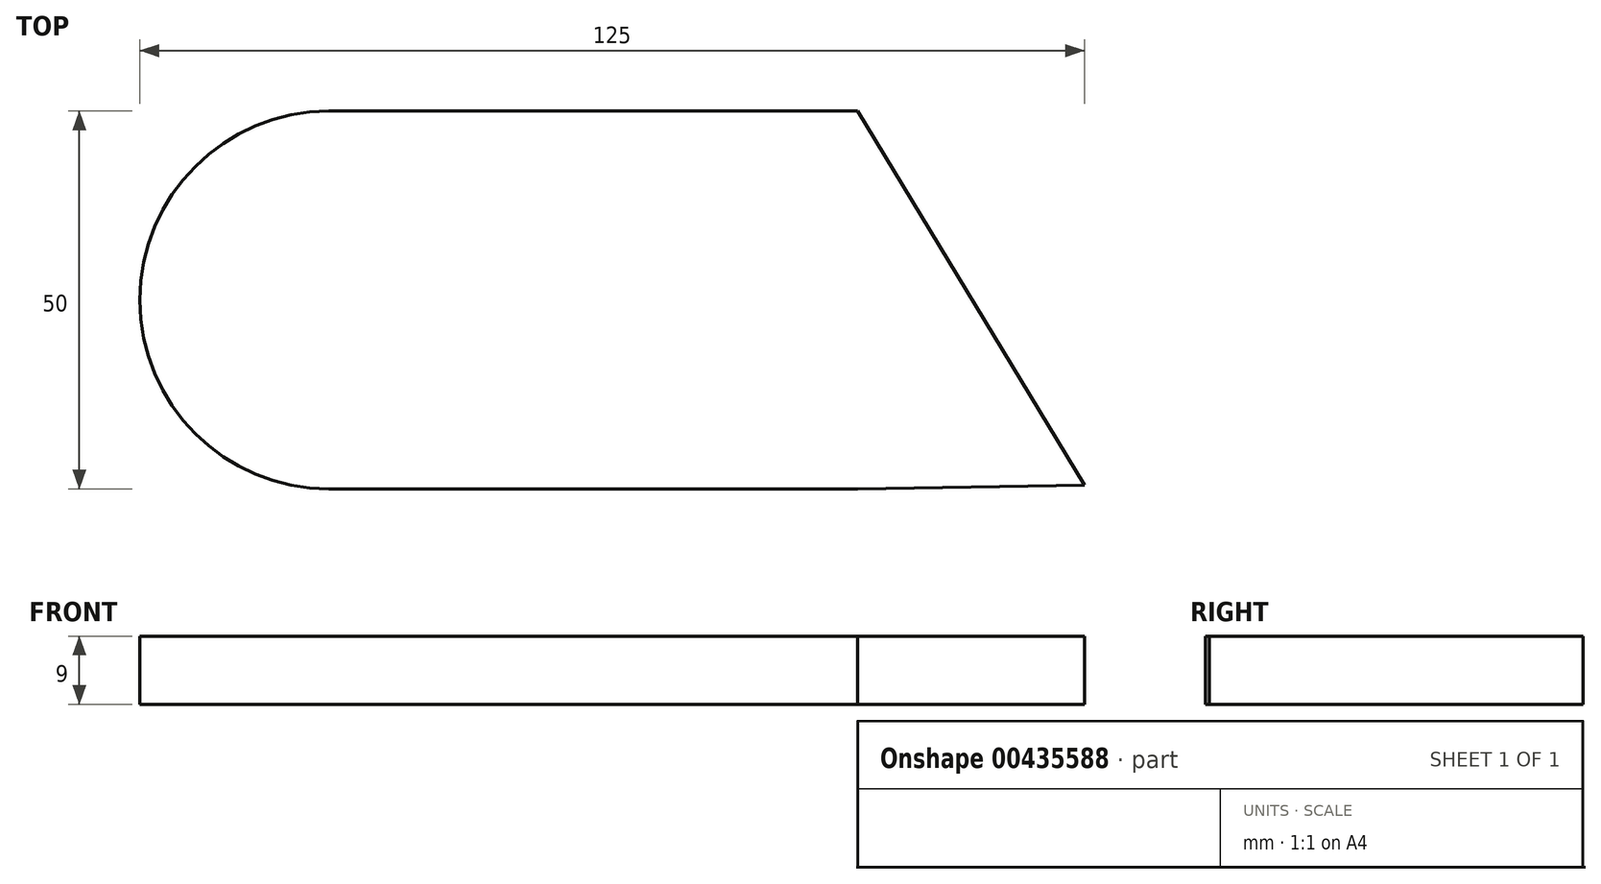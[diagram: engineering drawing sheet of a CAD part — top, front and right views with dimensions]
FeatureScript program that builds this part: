
annotation { "Feature Type Name" : "Feature", "Feature Type Description" : "" }
export const myFeature = defineFeature(function(context is Context, id is Id, definition is map)
    precondition{}
    {
        {
            var Q0;
            Q0=qCreatedBy(makeId("Top.planeOp"),FACE);
            var sketch = newSketch(context, id + "F0", { "sketchPlane" : qUnion([Q0])});
            skLineSegment(sketch, "E0.bottom", {"start": v(-28.66, 56.52) * mm, "end": v(41.34, 56.52) * mm});
            skLineSegment(sketch, "E0.top", {"start": v(-28.66, 6.52) * mm, "end": v(41.34, 6.52) * mm});
            skLineSegment(sketch, "E0.left", {"start": v(-28.66, 56.52) * mm, "end": v(-28.66, 6.52) * mm});
            skLineSegment(sketch, "E0.right", {"start": v(41.34, 56.52) * mm, "end": v(41.34, 6.52) * mm});
            skArc(sketch, "E1", {"start": v(-28.66, 56.52) * mm, "mid": v(-53.66, 31.52) * mm, "end": v(-28.66, 6.52) * mm});
            skLineSegment(sketch, "E2", {"start": v(41.34, 56.52) * mm, "end": v(71.34, 7.03) * mm});
            skLineSegment(sketch, "E3", {"start": v(41.34, 6.52) * mm, "end": v(71.34, 7.03) * mm});
            skSolve(sketch);
        }
        {
            var Q0;
            Q0=makeQuery(id+"F0.imprint","IMPRINT",FACE,{"disambiguationData":[TD([[makeQuery(id+"F0.imprint","IMPRINT",EDGE,{"derivedFrom":sQuery(id+"F0.wireOp",EDGE,"E0.bottom")}),-1.0]])]});
            var Q1;
            Q1=makeQuery(id+"F0.imprint","IMPRINT",FACE,{"disambiguationData":[TD([[makeQuery(id+"F0.imprint","IMPRINT",EDGE,{"derivedFrom":sQuery(id+"F0.wireOp",EDGE,"E0.left")}),-1.0]])]});
            var Q2;
            Q2=makeQuery(id+"F0.imprint","IMPRINT",FACE,{"disambiguationData":[TD([[makeQuery(id+"F0.imprint","IMPRINT",EDGE,{"derivedFrom":sQuery(id+"F0.wireOp",EDGE,"E0.right")}),1.0]])]});
            extrude(context, id + "F1", {"entities" : qUnion([Q0, Q1, Q2]), "depth" : 9 * mm});
        }
    });
